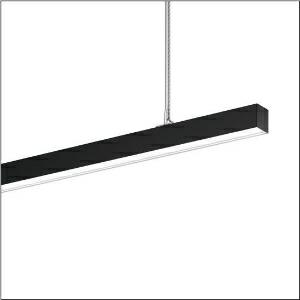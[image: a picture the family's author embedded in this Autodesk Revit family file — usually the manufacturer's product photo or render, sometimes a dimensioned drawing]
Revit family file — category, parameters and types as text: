
# Revit family: silica_r__21_51mx33dc3dbb_6d07
name_source: partatom
category: Lighting Fixtures
units: mm (PartAtom-declared; Revit-internal decimal feet)

## family parameters
Cut with Voids When Loaded = No
Host = Face
Light Source = No
Part Type = Normal
Room Calculation Point = No
Round Connector Dimension = Use Diameter
Shared = No

## types (1)
- --- (1 x LED, 14780 lm, 99.5 W, 3000K)
    Apparent Load = 100 VA
    CIE Flux Codes = 78 96 99 55 100
    Color Rendering = 80
    Color Temperature = 3000K
    Default Elevation = 1800 mm
    Description = Silica® 21, office luminaire, primary optical cover: prismatic diffuser, of PMMA, CAT 2 (L<= 3000cd/m²), light emission: direct/indirect distribution, primary light characteristic: symmetric, installation type: suspended mounting, LED, rated luminous flux: 14.780lm, luminous efficacy: 149lm/W, light colour: 830, colour temperature: 3000K, control gear: DALI 2, with terminal, 3+2-pole, max. 2.5mm², mains connection: 220..240V, AC, 50/60Hz, rated input power: 99.5W, luminaire housing, of aluminium, matt jet black (RAL 9005), length: 3.004mm, width: 53mm, height: 53mm, protection rating (complete): IP20, insulation class (complete): insulation class I (protective earthing), certification: CE, permissible operating ambient temperature: 0..+35°C, standard: EN 50419, packaging unit: 1 piece
    Height = 53 mm
    Lamp = 1 x LED
    Lamp Light Flux = 14780 lm
    Lamp Power = 99.5 W
    Lamp count = 1
    Length = 3004 mm
    Luminous efficacy = 149 lm/W
    Manufacturer = Siteco
    ModVariant = No
    Model = 51MX33DC3DBB
    Mounting Place = Ceiling
    Mounting Type = Pendant
    Number of Poles = 1
    OnlyDefault = Yes
    Power Factor = 1
    Product Name = Silica® 21
    Product group = office luminaire | ceiling pendant
    ProductGroupID = 903
    Protection Class = Protection class I
    Protection Degree = IP 20
    RLX_Detail_Level = 1
    RLX_Emergency_Light_Flux = 0 lm
    RLX_Emergency_Type = 0
    RLX_Emergency_Type_DB = No
    RlxData = <blob elided: 26257 chars, md5=bb20832c>
    Socket = socket
    Standby Power = 0 W
    System Light Flux = 14780 lm
    System Power = 100 W
    Type Comments = factory setting: luminous flux: 100 % | dim-lin: 254 | 345 mA
    Type Image = l_1335856.jpg
    URL = http://relux.com
    VarID = @adj_140149
    Voltage = 0 V
    Weight = 0.00 kg
    Width = 53 mm

## geometry (parser evidence)
native form markers: Blend x4, Sweep x14
no freeform markers — native parametric forms only
